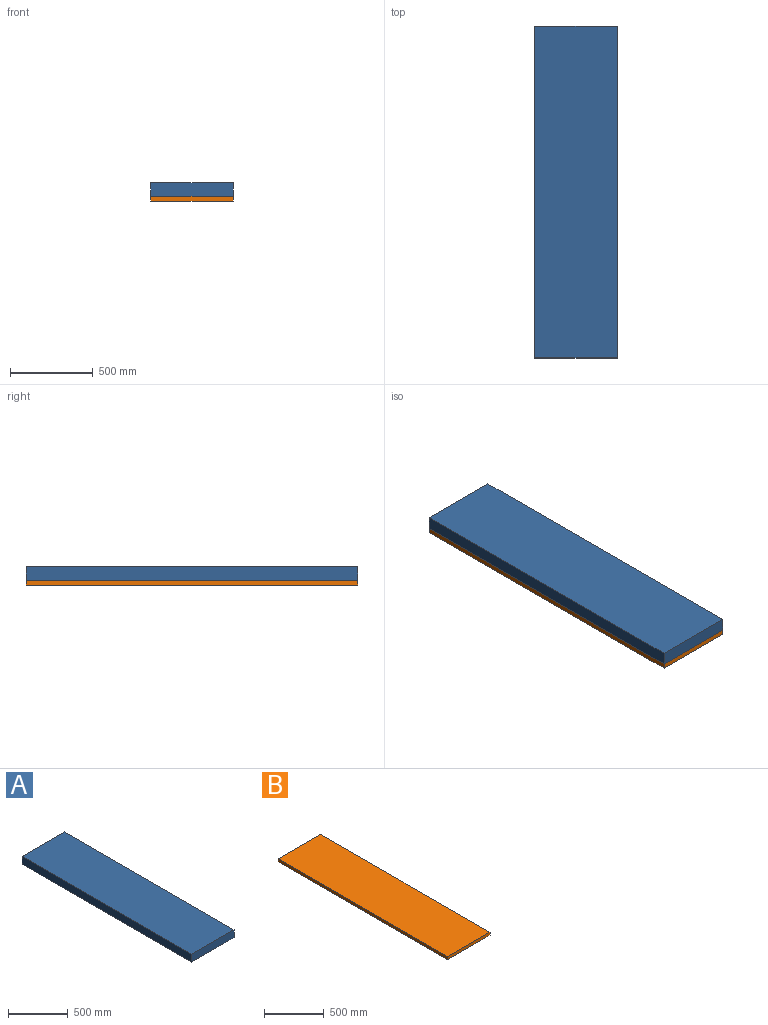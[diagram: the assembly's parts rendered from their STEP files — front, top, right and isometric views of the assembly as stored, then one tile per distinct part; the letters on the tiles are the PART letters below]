
ASSEMBLY  parts=2 mates=1
PART A: 6 faces, bbox 500x2000x80 mm
  f0: plane 2000x80mm, normal (1,0,0), area 160000mm2, adj f1,f3,f4,f5
  f1: plane 500x80mm, normal (0,1,0), area 40000mm2, adj f0,f2,f4,f5
  f2: plane 2000x80mm, normal (-1,0,0), area 160000mm2, adj f1,f3,f4,f5
  f3: plane 500x80mm, normal (0,-1,0), area 40000mm2, adj f0,f2,f4,f5
  f4: plane 2000x500mm, normal (0,0,1), area 1000000mm2, adj f0,f1,f2,f3
  f5: plane 2000x500mm, normal (0,0,-1), area 1000000mm2, adj f0,f1,f2,f3
PART B: 6 faces, bbox 500x2000x30 mm
  f0: plane 2000x30mm, normal (1,0,0), area 60000mm2, adj f1,f3,f4,f5
  f1: plane 500x30mm, normal (0,1,0), area 15000mm2, adj f0,f2,f4,f5
  f2: plane 2000x30mm, normal (-1,0,0), area 60000mm2, adj f1,f3,f4,f5
  f3: plane 500x30mm, normal (0,-1,0), area 15000mm2, adj f0,f2,f4,f5
  f4: plane 2000x500mm, normal (0,0,1), area 1000000mm2, adj f0,f1,f2,f3
  f5: plane 2000x500mm, normal (0,0,-1), area 1000000mm2, adj f0,f1,f2,f3
PLACE A t=(0,0,30)mm
PLACE B at identity fixed
MATE fastened A.f5 <-> B.f4  axis (0,0,-1) through (-250,-1000,30)mm
